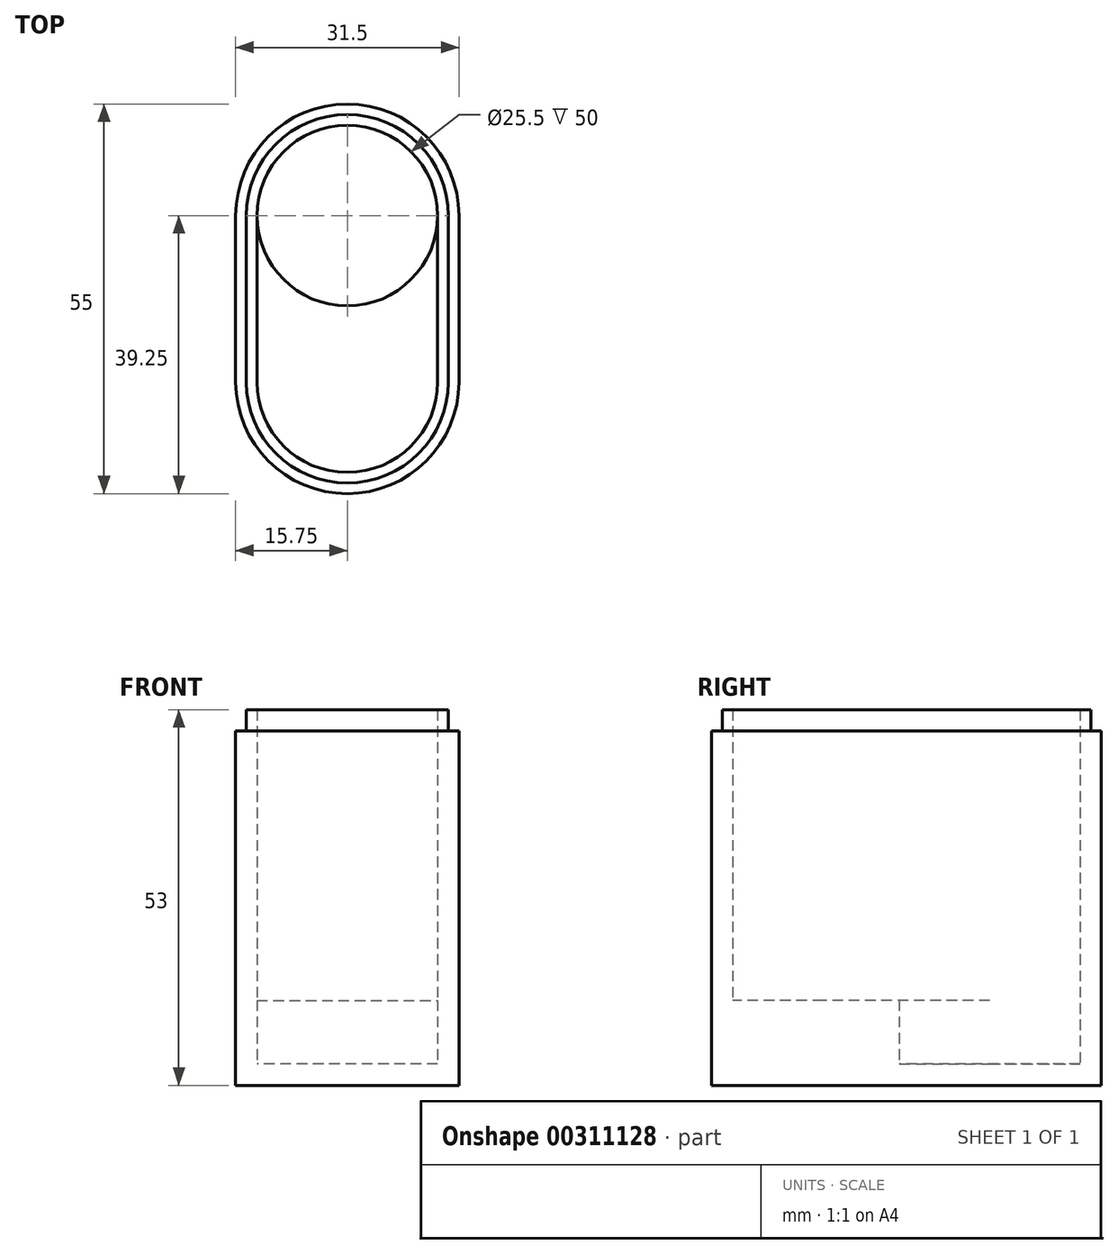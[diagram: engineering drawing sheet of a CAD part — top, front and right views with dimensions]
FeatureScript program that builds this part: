
annotation { "Feature Type Name" : "Feature", "Feature Type Description" : "" }
export const myFeature = defineFeature(function(context is Context, id is Id, definition is map)
    precondition{}
    {
        {
            var Q0;
            Q0=qCreatedBy(makeId("Top.planeOp"),FACE);
            var sketch = newSketch(context, id + "F0", { "sketchPlane" : qUnion([Q0])});
            skArc(sketch, "E0", {"start": v(12.75, 0) * mm, "mid": v(0, 12.75) * mm, "end": v(-12.75, 0) * mm});
            skLineSegment(sketch, "E1", {"start": v(12.75, 0) * mm, "end": v(12.75, 0) * mm});
            skLineSegment(sketch, "E2", {"start": v(-12.75, 0) * mm, "end": v(-12.75, -23.5) * mm});
            skLineSegment(sketch, "E3", {"start": v(-12.75, -23.5) * mm, "end": v(12.75, -23.5) * mm, "construction": true});
            skLineSegment(sketch, "E4", {"start": v(0, 0) * mm, "end": v(0, -23.5) * mm, "construction": true});
            skArc(sketch, "E5", {"start": v(-12.75, -23.5) * mm, "mid": v(0, -36.25) * mm, "end": v(12.75, -23.5) * mm});
            skLineSegment(sketch, "E6", {"start": v(12.75, 0) * mm, "end": v(12.75, -23.5) * mm});
            skArc(sketch, "E7.0", {"start": v(15.75, 0) * mm, "mid": v(0, 15.75) * mm, "end": v(-15.75, 0) * mm});
            skLineSegment(sketch, "E7.1", {"start": v(15.75, 0) * mm, "end": v(15.75, -23.5) * mm});
            skArc(sketch, "E7.2", {"start": v(-15.75, -23.5) * mm, "mid": v(0, -39.25) * mm, "end": v(15.75, -23.5) * mm});
            skLineSegment(sketch, "E7.3", {"start": v(-15.75, 0) * mm, "end": v(-15.75, -23.5) * mm});
            skCircle(sketch, "E8", {"center": v(0, 0) * mm, "radius": 12.75 * mm});
            skSolve(sketch);
        }
        {
            var Q0;
            Q0 = qSketchRegion(id + "F0", true);
            var Q1;
            {var subQ0=sQuery(id+"F0.wireOp",EDGE,"E8");var subQ1=makeQuery(id+"F0.imprint","INTERSECT",VERTEX,{"derivedFrom":[sQuery(id+"F0.wireOp",EDGE,"E2"),subQ0]});Q1=makeQuery(id+"F0.imprint","IMPRINT",FACE,{"disambiguationData":[TD([[makeQuery(id+"F0.imprint","IMPRINT",EDGE,{"disambiguationData":[TD([[subQ1,1.0]])],"derivedFrom":subQ0}),1.0]])]});}
            var Q2;
            {var subQ0=sQuery(id+"F0.wireOp",EDGE,"E2");Q2=makeQuery(id+"F0.imprint","IMPRINT",FACE,{"disambiguationData":[TD([[makeQuery(id+"F0.imprint","IMPRINT",EDGE,{"derivedFrom":subQ0}),1.0]])]});}
            extrude(context, id + "F1", {"entities" : qUnion([Q0, Q1, Q2]), "depth" : 3 * mm});
        }
        {
            var Q0;
            {var subQ0=sQuery(id+"F0.wireOp",EDGE,"E2");Q0=makeQuery(id+"F0.imprint","IMPRINT",FACE,{"disambiguationData":[TD([[makeQuery(id+"F0.imprint","IMPRINT",EDGE,{"derivedFrom":subQ0}),1.0]])]});}
            extrude(context, id + "F2", {"entities" : qUnion([Q0]), "operationType" : NewBodyOperationType.ADD, "depth" : 12 * mm});
        }
        {
            var Q0;
            {var subQ1=sQuery(id+"F0.wireOp",EDGE,"E2");Q0=makeQuery(id+"F0.imprint","IMPRINT",FACE,{"disambiguationData":[TD([[makeQuery(id+"F0.imprint","IMPRINT",EDGE,{"derivedFrom":subQ1}),-1.0]])]});}
            extrude(context, id + "F3", {"entities" : qUnion([Q0]), "operationType" : NewBodyOperationType.ADD, "depth" : 50 * mm});
        }
        {
            var Q0;
            Q0=makeQuery(id+"F3.opExtrude","CAP_FACE",FACE,{"disambiguationData":[OSD([sQuery(id+"F0.wireOp",EDGE,"E2"),sQuery(id+"F0.wireOp",EDGE,"E5"),sQuery(id+"F0.wireOp",EDGE,"E6"),sQuery(id+"F0.wireOp",EDGE,"E7.0"),sQuery(id+"F0.wireOp",EDGE,"E7.1"),sQuery(id+"F0.wireOp",EDGE,"E7.2"),sQuery(id+"F0.wireOp",EDGE,"E7.3"),sQuery(id+"F0.wireOp",EDGE,"E8")])],"isStart":false});
            var sketch = newSketch(context, id + "F4", { "sketchPlane" : qUnion([Q0])});
            skLineSegment(sketch, "E9.0", {"start": v(-14.25, 0) * mm, "end": v(-14.25, -23.5) * mm});
            skArc(sketch, "E9.1", {"start": v(14.25, 0) * mm, "mid": v(0, 14.25) * mm, "end": v(-14.25, 0) * mm});
            skLineSegment(sketch, "E9.2", {"start": v(14.25, 0) * mm, "end": v(14.25, -23.5) * mm});
            skArc(sketch, "E9.3", {"start": v(-14.25, -23.5) * mm, "mid": v(0, -37.75) * mm, "end": v(14.25, -23.5) * mm});
            skSolve(sketch);
        }
        {
            var Q0;
            Q0=makeQuery(id+"F4.imprint","IMPRINT",FACE,{"disambiguationData":[TD([[makeQuery(id+"F4.imprint","IMPRINT",EDGE,{"derivedFrom":sQuery(id+"F4.wireOp",EDGE,"E9.0")}),1.0]])]});
            extrude(context, id + "F5", {"entities" : qUnion([Q0]), "operationType" : NewBodyOperationType.ADD, "depth" : 3 * mm});
        }
    });
